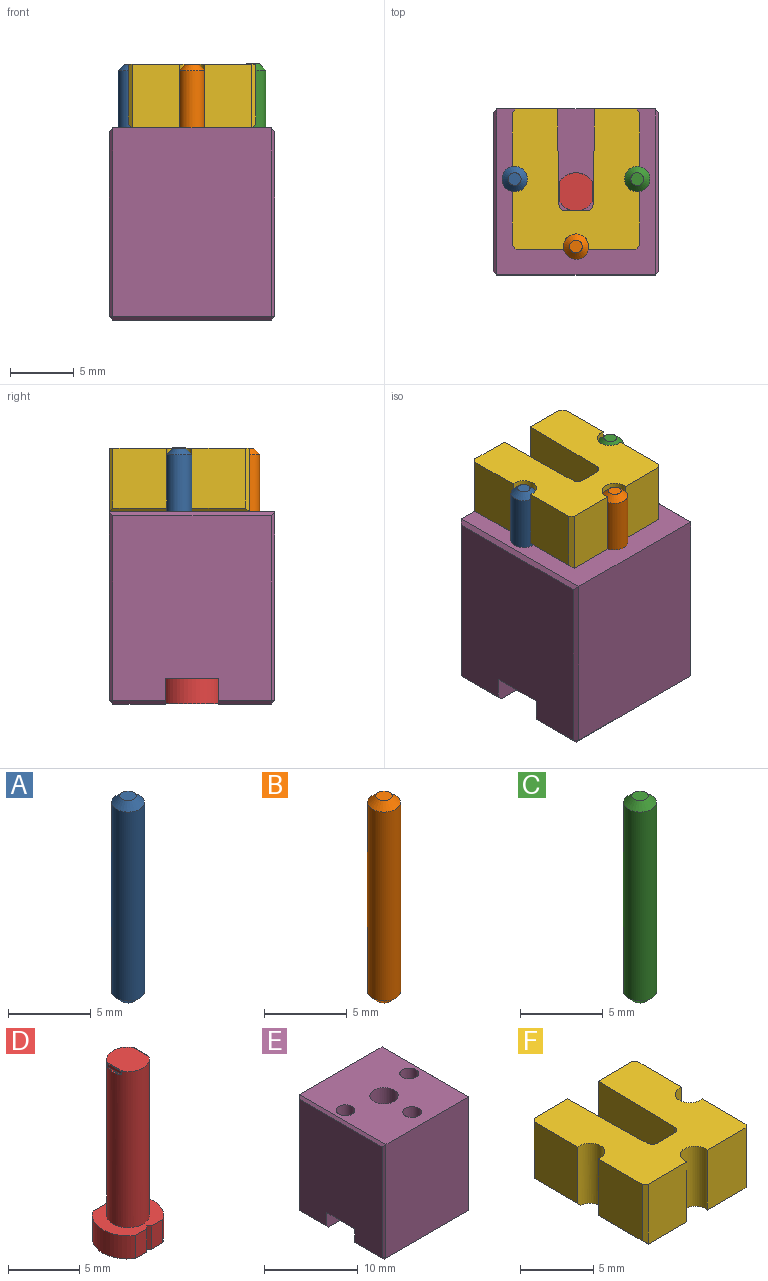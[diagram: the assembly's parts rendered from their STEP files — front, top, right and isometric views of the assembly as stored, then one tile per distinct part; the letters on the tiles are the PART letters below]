
ASSEMBLY  parts=6 mates=9
PART A: 5 faces, bbox 2x2x15 mm
  f0: cylinder r=1mm len=14mm, axis (0,0,1), area 88mm2, adj f3,f4
  f1: plane 1x1mm, normal (0,0,-1), area 0.8mm2, adj f3
  f2: plane 1x1mm, normal (0,0,1), area 0.8mm2, adj f4
  f3: cone r=1mm half-angle=45deg, axis (0,0,1), area 3.3mm2, adj f0,f1
  f4: cone r=0.5mm half-angle=45deg, axis (0,0,-1), area 3.3mm2, adj f0,f2
PART B: 5 faces, bbox 2x2x15 mm
  f0: cylinder r=1mm len=14mm, axis (0,0,1), area 88mm2, adj f3,f4
  f1: plane 1x1mm, normal (0,0,-1), area 0.8mm2, adj f3
  f2: plane 1x1mm, normal (0,0,1), area 0.8mm2, adj f4
  f3: cone r=1mm half-angle=45deg, axis (0,0,1), area 3.3mm2, adj f0,f1
  f4: cone r=0.5mm half-angle=45deg, axis (0,0,-1), area 3.3mm2, adj f0,f2
PART C: 5 faces, bbox 2x2x15 mm
  f0: cylinder r=1mm len=14mm, axis (0,0,1), area 88mm2, adj f3,f4
  f1: plane 1x1mm, normal (0,0,-1), area 0.8mm2, adj f3
  f2: plane 1x1mm, normal (0,0,1), area 0.8mm2, adj f4
  f3: cone r=1mm half-angle=45deg, axis (0,0,1), area 3.3mm2, adj f0,f1
  f4: cone r=0.5mm half-angle=45deg, axis (0,0,-1), area 3.3mm2, adj f0,f2
PART D: 19 faces, bbox 5x4.2x15.4 mm
  f0: cylinder r=1.5mm len=13.43mm, axis (0,0,1), area 125.6mm2, adj f1,f2,f11,f12,f13,f14,f15,f16
  f1: plane 3x2.61mm, normal (0,0,1), area 6.6mm2, adj f0,f15,f16
  f2: plane 5x4.2mm, normal (0,0,1), area 11mm2, adj f0,f3,f4,f5,f7,f8,f9,f10
  f3: plane 2x1.11mm, normal (0,-1,0), area 2.2mm2, adj f2,f4,f6,f10
  f4: cylinder r=2.5mm len=4.2mm, axis (0,0,-1), area 10mm2, adj f2,f3,f6,f8
  f5: cylinder r=2.5mm len=4.2mm, axis (0,0,-1), area 10mm2, adj f2,f6,f7,f8
  f6: plane 5x4.2mm, normal (0,0,-1), area 18.1mm2, adj f3,f4,f5,f7,f8,f9,f10
  f7: plane 2x1.11mm, normal (0,-1,0), area 2.2mm2, adj f2,f5,f6,f9
  f8: plane 2.71x2mm, normal (0,1,0), area 5.4mm2, adj f2,f4,f5,f6
  f9: plane 2x0.25mm, normal (-0.71,-0.71,0), area 0.7mm2, adj f2,f6,f7,f10
  f10: plane 2x0.25mm, normal (0.71,-0.71,0), area 0.7mm2, adj f2,f3,f6,f9
  f11: plane 1.34x0.26mm, normal (1,-0.02,0.03), area 0.3mm2, adj f0,f16,f17
  f12: plane 1.07x0.11mm, normal (0,0,1), area 0.1mm2, adj f0,f17
  f13: plane 1.34x0.26mm, normal (-1,-0.02,0.03), area 0.3mm2, adj f0,f15,f18
  f14: plane 1.07x0.11mm, normal (0,0,1), area 0.1mm2, adj f0,f18
  f15: plane 1.53x0.08mm, normal (-0.69,-0.01,0.72), area 0.1mm2, adj f0,f1,f13
  f16: plane 1.53x0.08mm, normal (0.69,-0.01,0.72), area 0.1mm2, adj f0,f1,f11
  f17: cylinder r=0.05mm len=1.31mm, axis (0.02,1,0), area 0.1mm2, adj f0,f11,f12
  f18: cylinder r=0.05mm len=1.31mm, axis (-0.02,1,0), area 0.1mm2, adj f0,f13,f14
PART E: 32 faces, bbox 13x13x15.1 mm
  f0: plane 12.4x4.1mm, normal (0,0,-1), area 50.8mm2, adj f9,f23,f26,f29
  f1: plane 14.47x12.4mm, normal (-1,0,0), area 172.2mm2, adj f8,f9,f12,f18,f19,f27,f29,f30
  f2: cylinder r=1.5mm len=13.05mm, axis (0,0,1), area 123mm2, adj f7,f12
  f3: plane 12.4x4.1mm, normal (0,0,-1), area 47.6mm2, adj f8,f10,f11,f15,f17,f18,f22
  f4: plane 14.77x12.4mm, normal (0,1,0), area 183.2mm2, adj f7,f24,f26,f27
  f5: plane 14.47x12.4mm, normal (1,0,0), area 172.2mm2, adj f9,f10,f12,f16,f17,f23,f24,f31
  f6: plane 14.77x12.4mm, normal (0,-1,0), area 183.2mm2, adj f7,f16,f19,f22
  f7: plane 13x12.4mm, normal (0,0,1), area 144.7mm2, adj f2,f4,f6,f13,f14,f15,f30,f31
  f8: plane 6.25x2.02mm, normal (0,1,0), area 12.6mm2, adj f1,f3,f11,f12,f18
  f9: plane 13x2.02mm, normal (0,-1,0), area 26.2mm2, adj f0,f1,f5,f12,f23,f29
  f10: plane 6.25x2.02mm, normal (0,1,0), area 12.6mm2, adj f3,f5,f11,f12,f17
  f11: cylinder r=0.25mm len=2.02mm, axis (0,0,-1), area 1.6mm2, adj f3,f8,f10,f12
  f12: plane 13x4.45mm, normal (0,0,-1), area 41.3mm2, adj f1,f2,f5,f8,f9,f10,f11,f13
  f13: cylinder r=1mm len=13.05mm, axis (0,0,1), area 82mm2, adj f7,f12
  f14: cylinder r=1mm len=13.05mm, axis (0,0,1), area 82mm2, adj f7,f12
  f15: cylinder r=1mm len=15.07mm, axis (0,0,1), area 94.7mm2, adj f3,f7
  f16: plane 14.77x0.3mm, normal (0.71,-0.71,0), area 6.2mm2, adj f5,f6,f20,f31
  f17: plane 4.1x0.3mm, normal (0.71,0,-0.71), area 1.7mm2, adj f3,f5,f10,f20
  f18: plane 4.1x0.3mm, normal (-0.71,0,-0.71), area 1.7mm2, adj f1,f3,f8,f21
  f19: plane 14.77x0.3mm, normal (-0.71,-0.71,0), area 6.2mm2, adj f1,f6,f21,f30
  f20: plane 0.3x0.3mm, normal (0.58,-0.58,-0.58), area 0.1mm2, adj f16,f17,f22
  f21: plane 0.3x0.3mm, normal (-0.58,-0.58,-0.58), area 0.1mm2, adj f18,f19,f22
  f22: plane 12.4x0.3mm, normal (0,-0.71,-0.71), area 5.3mm2, adj f3,f6,f20,f21
  f23: plane 4.1x0.3mm, normal (0.71,0,-0.71), area 1.7mm2, adj f0,f5,f9,f25
  f24: plane 14.77x0.3mm, normal (0.71,0.71,0), area 6.2mm2, adj f4,f5,f25,f31
  f25: plane 0.3x0.3mm, normal (0.58,0.58,-0.58), area 0.1mm2, adj f23,f24,f26
  f26: plane 12.4x0.3mm, normal (0,0.71,-0.71), area 5.3mm2, adj f0,f4,f25,f28
  f27: plane 14.77x0.3mm, normal (-0.71,0.71,0), area 6.2mm2, adj f1,f4,f28,f30
  f28: plane 0.3x0.3mm, normal (-0.58,0.58,-0.58), area 0.1mm2, adj f26,f27,f29
  f29: plane 4.1x0.3mm, normal (-0.71,0,-0.71), area 1.7mm2, adj f0,f1,f9,f28
  f30: plane 13x0.3mm, normal (-0.71,0,0.71), area 5.4mm2, adj f1,f7,f19,f27
  f31: plane 13x0.3mm, normal (0.71,0,0.71), area 5.4mm2, adj f5,f7,f16,f24
PART F: 31 faces, bbox 10x11x5 mm
  f0: plane 4.7x4.22mm, normal (1,0,0), area 19.8mm2, adj f13,f20,f29,f30
  f1: plane 4.7x4.22mm, normal (-1,0,0), area 19.8mm2, adj f13,f21,f23,f24
  f2: plane 5x3.72mm, normal (0,-1,0), area 18.6mm2, adj f13,f14,f22,f23
  f3: plane 4.7x4.22mm, normal (1,0,0), area 19.8mm2, adj f13,f20,f27,f28
  f4: plane 5x3.23mm, normal (0,1,0), area 16.1mm2, adj f5,f13,f14,f16,f27
  f5: plane 7.51x4.93mm, normal (-1,0.02,0), area 37mm2, adj f4,f6,f13,f16
  f6: cylinder r=0.5mm len=4.93mm, axis (0,0,-1), area 3.8mm2, adj f5,f7,f13,f18
  f7: plane 4.93x1.67mm, normal (0,1,0), area 8.2mm2, adj f6,f8,f13,f19
  f8: cylinder r=0.5mm len=4.93mm, axis (0,0,-1), area 3.8mm2, adj f7,f9,f13,f17
  f9: plane 7.51x4.93mm, normal (1,0.02,0), area 37mm2, adj f8,f10,f13,f15
  f10: plane 5x3.23mm, normal (0,1,0), area 16.1mm2, adj f9,f13,f14,f15,f25
  f11: plane 4.7x4.22mm, normal (-1,0,0), area 19.8mm2, adj f13,f21,f25,f26
  f12: plane 5x3.72mm, normal (0,-1,0), area 18.6mm2, adj f13,f14,f22,f29
  f13: plane 11x10mm, normal (0,0,1), area 81.7mm2, adj f0,f1,f2,f3,f4,f5,f6,f7
  f14: plane 11x9.4mm, normal (0,0,-1), area 75mm2, adj f2,f4,f10,f12,f15,f16,f17,f18
  f15: cylinder r=0.07mm len=7.51mm, axis (-0.02,1,0), area 0.9mm2, adj f9,f10,f14,f17
  f16: cylinder r=0.07mm len=7.51mm, axis (-0.02,-1,0), area 0.9mm2, adj f4,f5,f14,f18
  f17: torus R=0.57mm, axis (0,0,1), area 0.1mm2, adj f8,f14,f15,f19
  f18: torus R=0.57mm, axis (0,0,1), area 0.1mm2, adj f6,f14,f16,f19
  f19: cylinder r=0.07mm len=1.67mm, axis (-1,0,0), area 0.2mm2, adj f7,f14,f17,f18
  f20: cylinder r=1mm len=5mm, axis (0,0,1), area 17.6mm2, adj f0,f3,f13,f14,f28,f30
  f21: cylinder r=1mm len=5mm, axis (0,0,1), area 17.6mm2, adj f1,f11,f13,f14,f24,f26
  f22: cylinder r=1mm len=5mm, axis (0,0,1), area 17.7mm2, adj f2,f12,f13,f14
  f23: plane 5x0.3mm, normal (-0.71,-0.71,0), area 2.1mm2, adj f1,f2,f13,f24
  f24: plane 4.52x0.3mm, normal (-0.71,0,-0.71), area 1.8mm2, adj f1,f14,f21,f23
  f25: plane 5x0.3mm, normal (-0.71,0.71,0), area 2.1mm2, adj f10,f11,f13,f26
  f26: plane 4.52x0.3mm, normal (-0.71,0,-0.71), area 1.8mm2, adj f11,f14,f21,f25
  f27: plane 5x0.3mm, normal (0.71,0.71,0), area 2.1mm2, adj f3,f4,f13,f28
  f28: plane 4.52x0.3mm, normal (0.71,0,-0.71), area 1.8mm2, adj f3,f14,f20,f27
  f29: plane 5x0.3mm, normal (0.71,-0.71,0), area 2.1mm2, adj f0,f12,f13,f30
  f30: plane 4.52x0.3mm, normal (0.71,0,-0.71), area 1.8mm2, adj f0,f14,f20,f29
PLACE A t=(2.57,2.94,0)mm
PLACE B t=(2.57,2.94,0)mm
PLACE C t=(2.57,2.94,0.03)mm
PLACE D t=(-12.52,-1.55,12.14)mm fixed
PLACE E t=(-11.88,3.82,11.91)mm
PLACE F t=(-11.88,3.82,11.91)mm
MATE planar E.f2 <-> F.f14  axis (0,0,1) through (-12.52,-1.55,11.77)mm
MATE slider C.f0 <-> E.f14  axis (0,0,1) through (-7.72,-0.55,9.3)mm
MATE fastened E.f14 <-> F.f20  axis (0,0,1) through (-7.72,-0.55,11.77)mm
MATE fastened A.f0 <-> F.f21  axis (0,0,1) through (-17.32,-0.55,16.77)mm
MATE slider D.f0 <-> E.f2  axis (0,0,1) through (-12.52,-1.55,-1.28)mm
MATE fastened D.f0 <-> E.f2  axis (0,0,1) through (-12.52,-1.55,-1.28)mm
MATE planar F.f13 <-> F.f20  axis (0,0,1) through (-12.52,-0.86,16.77)mm
MATE fastened B.f0 <-> F.f22  axis (0,0,1) through (-12.52,-5.85,16.77)mm
MATE cylindrical D.f0 <-> E.f2  axis (0,0,1) through (-12.52,-1.55,5.43)mm
